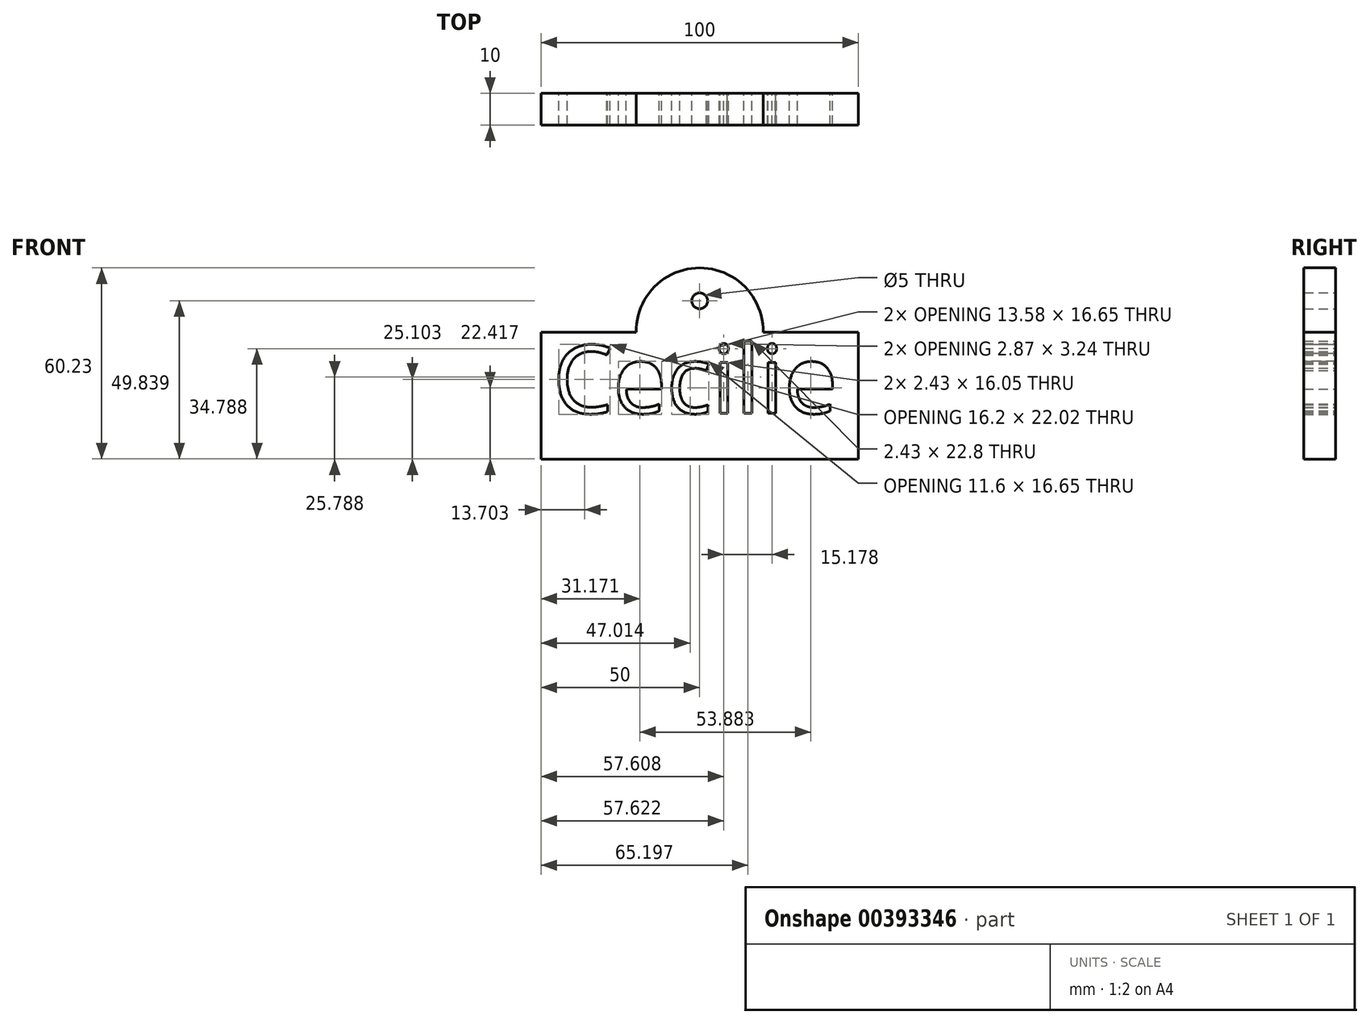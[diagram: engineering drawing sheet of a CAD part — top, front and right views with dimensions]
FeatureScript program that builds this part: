
annotation { "Feature Type Name" : "Feature", "Feature Type Description" : "" }
export const myFeature = defineFeature(function(context is Context, id is Id, definition is map)
    precondition{}
    {
        {
            var Q0;
            Q0=qCreatedBy(makeId("Front.planeOp"),FACE);
            var sketch = newSketch(context, id + "F0", { "sketchPlane" : qUnion([Q0])});
            skLineSegment(sketch, "E0.top", {"start": v(-50, 20.93) * mm, "end": v(50, 20.93) * mm});
            skLineSegment(sketch, "E0.left", {"start": v(-50, 60.93) * mm, "end": v(-50, 20.93) * mm});
            skLineSegment(sketch, "E0.right", {"start": v(50, 60.93) * mm, "end": v(50, 20.93) * mm});
            skPoint(sketch, "E1", {"position": v(0, 60.93) * mm});
            skPoint(sketch, "E2", {"position": v(-20, 60.93) * mm});
            skPoint(sketch, "E3", {"position": v(20, 60.93) * mm});
            skArc(sketch, "E4", {"start": v(20, 60.93) * mm, "mid": v(0, 81.16) * mm, "end": v(-20, 60.93) * mm});
            skLineSegment(sketch, "E5", {"start": v(-50, 60.93) * mm, "end": v(-20, 60.93) * mm});
            skLineSegment(sketch, "E6", {"start": v(20, 60.93) * mm, "end": v(50, 60.93) * mm});
            skCircle(sketch, "E7", {"center": v(0, 70.77) * mm, "radius": 2.5 * mm});
            skText(sketch, "E8", { "text": "Cecilie ", "fontName": "OpenSans-Regular.ttf"});
            const initialGuessF0  = {"E8": [-0.04623, 0.03532, 1, 0, 0.0216]};
            skSetInitialGuess(sketch, initialGuessF0);
            skSolve(sketch);
        }
        {
            var Q0;
            Q0=makeQuery(id+"F0.imprint","IMPRINT",FACE,{"disambiguationData":[TD([[makeQuery(id+"F0.imprint","IMPRINT",EDGE,{"derivedFrom":sQuery(id+"F0.wireOp",EDGE,"E0.top")}),1.0]])]});
            extrude(context, id + "F1", {"entities" : qUnion([Q0]), "depth" : 10 * mm});
        }
    });
